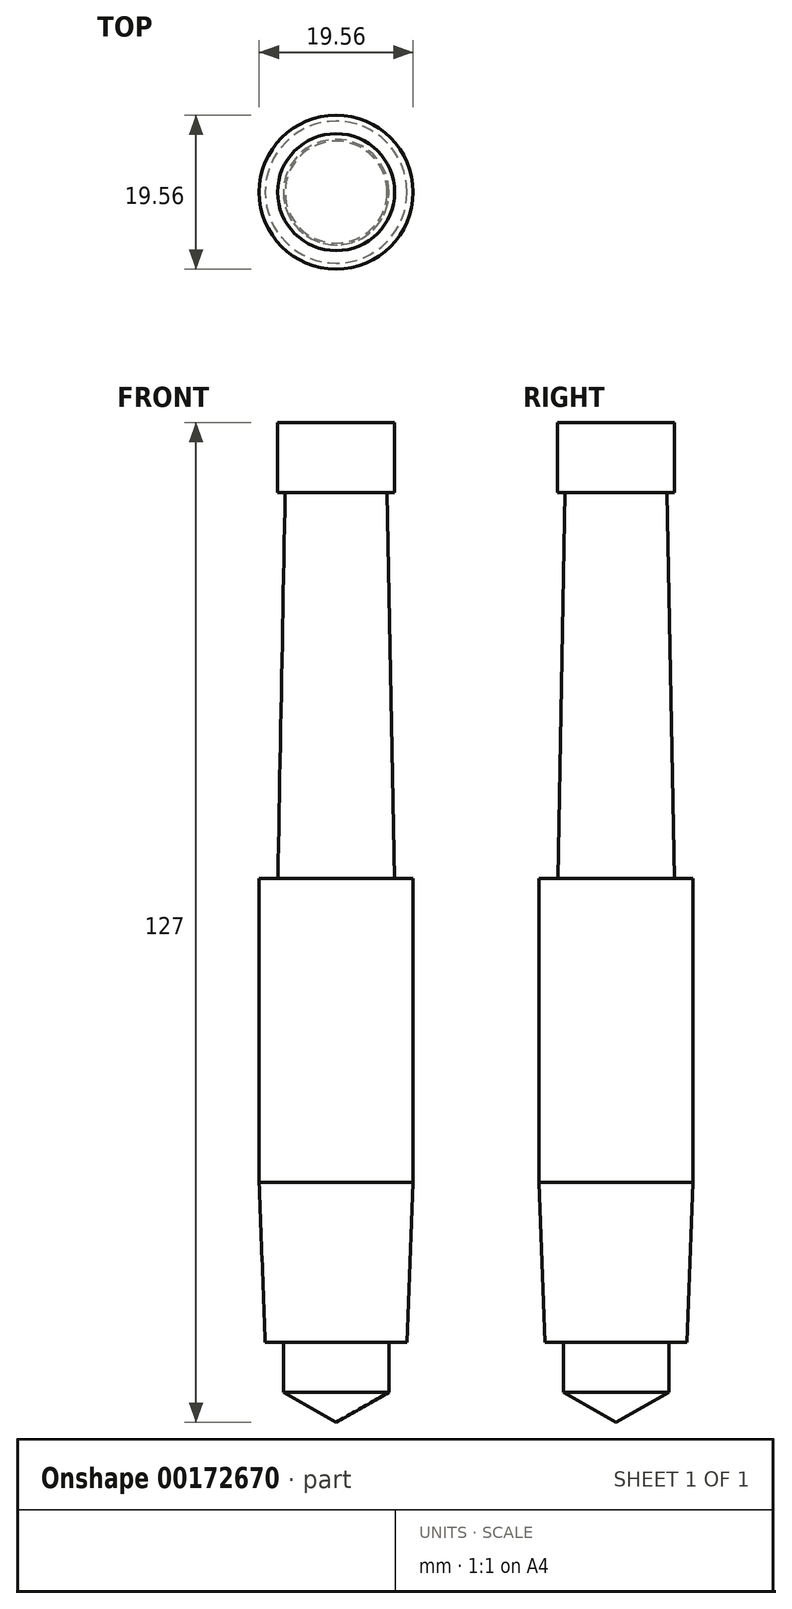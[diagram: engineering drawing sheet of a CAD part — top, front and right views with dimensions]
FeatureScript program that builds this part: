
annotation { "Feature Type Name" : "Feature", "Feature Type Description" : "" }
export const myFeature = defineFeature(function(context is Context, id is Id, definition is map)
    precondition{}
    {
        {
            var Q0;
            Q0=qCreatedBy(makeId("Front.planeOp"),FACE);
            var sketch = newSketch(context, id + "F0", { "sketchPlane" : qUnion([Q0])});
            skLineSegment(sketch, "E0", {"start": v(0, 0) * mm, "end": v(0, 127) * mm});
            skLineSegment(sketch, "E1", {"start": v(0, 127) * mm, "end": v(7.43, 127) * mm});
            skLineSegment(sketch, "E2", {"start": v(7.43, 127) * mm, "end": v(7.43, 118.11) * mm});
            skLineSegment(sketch, "E3", {"start": v(7.43, 118.11) * mm, "end": v(6.48, 118.11) * mm});
            skLineSegment(sketch, "E4", {"start": v(6.48, 118.11) * mm, "end": v(7.4, 69.09) * mm});
            skLineSegment(sketch, "E5", {"start": v(7.4, 69.09) * mm, "end": v(9.78, 69.09) * mm});
            skLineSegment(sketch, "E6", {"start": v(9.78, 69.09) * mm, "end": v(9.78, 30.48) * mm});
            skLineSegment(sketch, "E7", {"start": v(9.02, 10.16) * mm, "end": v(6.7, 10.16) * mm});
            skLineSegment(sketch, "E8", {"start": v(6.7, 10.16) * mm, "end": v(6.7, 3.81) * mm});
            skLineSegment(sketch, "E9", {"start": v(6.7, 3.81) * mm, "end": v(0, 0) * mm});
            skLineSegment(sketch, "E10", {"start": v(9.78, 30.48) * mm, "end": v(9.02, 10.16) * mm});
            skSolve(sketch);
        }
        {
            var Q0;
            Q0 = qSketchRegion(id + "F0", true);
            var Q1;
            Q1=sQuery(id+"F0.wireOp",EDGE,"E0");
            revolve(context, id + "F1", {"entities" : qUnion([Q0]), "axis" : qUnion([Q1]), "revolveType" : RevolveType.FULL});
        }
    });
